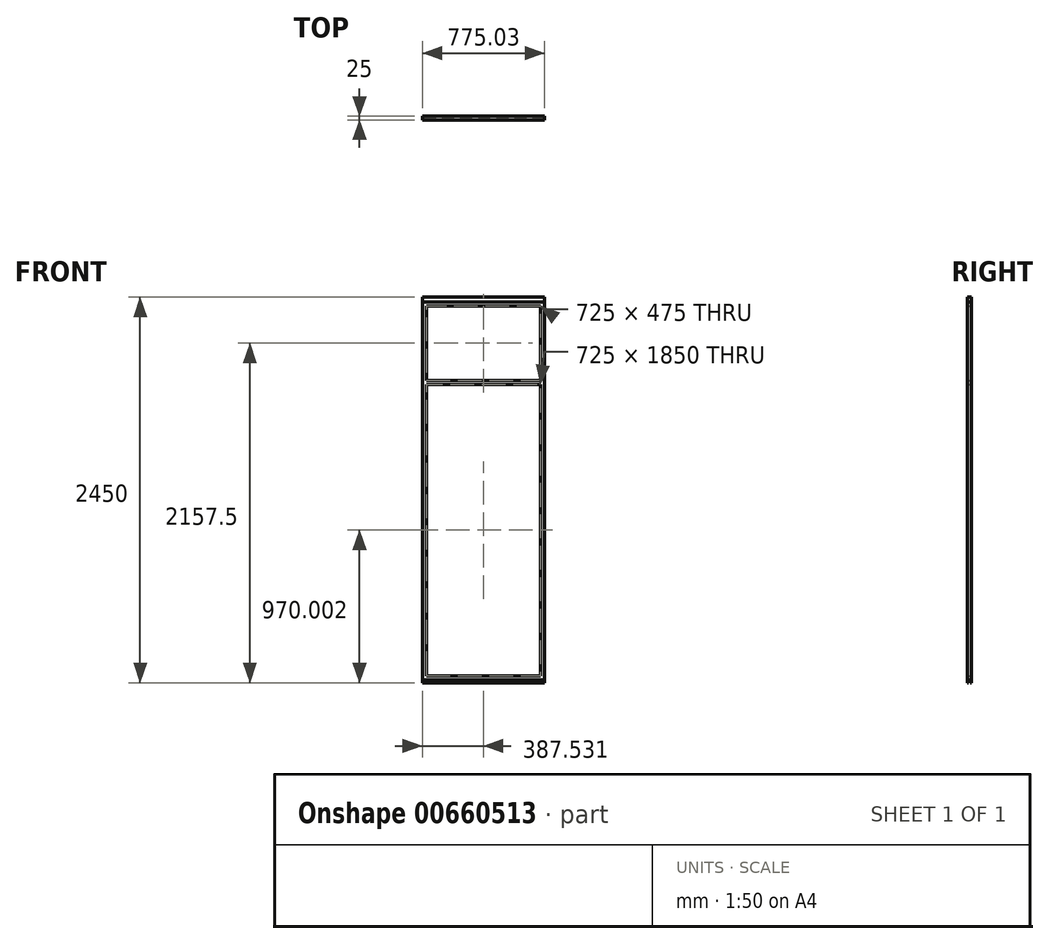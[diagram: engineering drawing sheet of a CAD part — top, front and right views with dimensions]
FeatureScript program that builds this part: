
annotation { "Feature Type Name" : "Feature", "Feature Type Description" : "" }
export const myFeature = defineFeature(function(context is Context, id is Id, definition is map)
    precondition{}
    {
        {
            var Q0;
            Q0=qCreatedBy(makeId("Front.planeOp"),FACE);
            var sketch = newSketch(context, id + "F0", { "sketchPlane" : qUnion([Q0])});
            skLineSegment(sketch, "E0", {"start": v(-1447.05, 238.44) * mm, "end": v(-722.05, 238.44) * mm});
            skLineSegment(sketch, "E1", {"start": v(-1472.05, 738.44) * mm, "end": v(-1472.05, 238.44) * mm});
            skLineSegment(sketch, "E2", {"start": v(-1472.05, 238.44) * mm, "end": v(-1472.05, -1661.56) * mm});
            skPoint(sketch, "E3", {"position": v(-697.05, 738.44) * mm});
            skLineSegment(sketch, "E4", {"start": v(-1472.05, 738.44) * mm, "end": v(-697.05, 738.44) * mm});
            skLineSegment(sketch, "E5", {"start": v(-697.05, 713.44) * mm, "end": v(-697.05, 238.44) * mm});
            skLineSegment(sketch, "E6.0", {"start": v(-1447.05, 713.44) * mm, "end": v(-1447.05, 238.44) * mm});
            skLineSegment(sketch, "E6.1", {"start": v(-1447.05, 213.44) * mm, "end": v(-1447.05, -1636.56) * mm});
            skLineSegment(sketch, "E6.5", {"start": v(-1447.05, 713.44) * mm, "end": v(-722.05, 713.44) * mm});
            skLineSegment(sketch, "E6.6", {"start": v(-1447.05, -1636.56) * mm, "end": v(-722.05, -1636.56) * mm});
            skLineSegment(sketch, "E7.0", {"start": v(-722.05, 713.44) * mm, "end": v(-722.05, 238.44) * mm});
            skLineSegment(sketch, "E8.0", {"start": v(-1447.05, 213.44) * mm, "end": v(-722.05, 213.44) * mm});
            skLineSegment(sketch, "E9.trimOffspring", {"start": v(-697.05, 213.44) * mm, "end": v(-697.05, -1636.56) * mm});
            skLineSegment(sketch, "E10.trimOffspring", {"start": v(-722.05, 213.44) * mm, "end": v(-722.05, -1636.56) * mm});
            skLineSegment(sketch, "E11", {"start": v(-1472.05, -1661.56) * mm, "end": v(-697.05, -1661.56) * mm});
            skLineSegment(sketch, "E12", {"start": v(-697.05, -1636.56) * mm, "end": v(-697.05, -1661.56) * mm});
            skLineSegment(sketch, "E13", {"start": v(-697.05, 738.44) * mm, "end": v(-697.05, 713.44) * mm});
            skLineSegment(sketch, "E14", {"start": v(-697.05, 238.44) * mm, "end": v(-697.05, 213.44) * mm});
            skSolve(sketch);
        }
        {
            var Q0;
            Q0=makeQuery(id+"F0.imprint","IMPRINT",FACE,{"disambiguationData":[TD([[makeQuery(id+"F0.imprint","IMPRINT",EDGE,{"derivedFrom":sQuery(id+"F0.wireOp",EDGE,"E0")}),-1.0]])]});
            extrude(context, id + "F1", {"entities" : qUnion([Q0]), "depth" : 25 * mm, "offsetDistance" : 25 * mm});
        }
        {
            var Q0;
            Q0=makeQuery(id+"F1.opExtrude","CAP_FACE",FACE,{"disambiguationData":[OSD([sQuery(id+"F0.wireOp",EDGE,"E0"),sQuery(id+"F0.wireOp",EDGE,"E1"),sQuery(id+"F0.wireOp",EDGE,"E2"),sQuery(id+"F0.wireOp",EDGE,"E4"),sQuery(id+"F0.wireOp",EDGE,"E5"),sQuery(id+"F0.wireOp",EDGE,"E6.0"),sQuery(id+"F0.wireOp",EDGE,"E6.1"),sQuery(id+"F0.wireOp",EDGE,"E6.5"),sQuery(id+"F0.wireOp",EDGE,"E6.6"),sQuery(id+"F0.wireOp",EDGE,"E7.0"),sQuery(id+"F0.wireOp",EDGE,"E8.0"),sQuery(id+"F0.wireOp",EDGE,"E9.trimOffspring"),sQuery(id+"F0.wireOp",EDGE,"E10.trimOffspring"),sQuery(id+"F0.wireOp",EDGE,"E11"),sQuery(id+"F0.wireOp",EDGE,"E12"),sQuery(id+"F0.wireOp",EDGE,"E13"),sQuery(id+"F0.wireOp",EDGE,"E14")])],"isStart":true});
            var sketch = newSketch(context, id + "F2", { "sketchPlane" : qUnion([Q0])});
            skLineSegment(sketch, "E15.bottom", {"start": v(697.05, -1661.56) * mm, "end": v(1472.08, -1661.56) * mm});
            skLineSegment(sketch, "E15.top", {"start": v(697.05, -1681.56) * mm, "end": v(1472.08, -1681.56) * mm});
            skLineSegment(sketch, "E15.left", {"start": v(697.05, -1661.56) * mm, "end": v(697.05, -1681.56) * mm});
            skLineSegment(sketch, "E15.right", {"start": v(1472.08, -1661.56) * mm, "end": v(1472.08, -1681.56) * mm});
            skSolve(sketch);
        }
        {
            var Q0;
            Q0 = qSketchRegion(id + "F2", true);
            extrude(context, id + "F3", {"entities" : qUnion([Q0]), "oppositeDirection" : true, "depth" : 25 * mm, "offsetDistance" : 25 * mm});
        }
        {
            var Q0;
            Q0=makeQuery(id+"F3.opExtrude","SWEPT_FACE",FACE,{"disambiguationData":[OSD([sQuery(id+"F2.wireOp",EDGE,"E15.right")])]});
            var sketch = newSketch(context, id + "F4", { "sketchPlane" : qUnion([Q0])});
            skLineSegment(sketch, "E16", {"start": v(12.5, -1681.56) * mm, "end": v(12.5, -1666.56) * mm, "construction": true});
            skLineSegment(sketch, "E17.bottom", {"start": v(6.5, -1666.56) * mm, "end": v(18.5, -1666.56) * mm});
            skLineSegment(sketch, "E17.top", {"start": v(6.5, -1681.56) * mm, "end": v(18.5, -1681.56) * mm});
            skLineSegment(sketch, "E17.left", {"start": v(6.5, -1666.56) * mm, "end": v(6.5, -1681.56) * mm});
            skLineSegment(sketch, "E17.right", {"start": v(18.5, -1666.56) * mm, "end": v(18.5, -1681.56) * mm});
            skPoint(sketch, "E18", {"position": v(12.5, -1681.56) * mm});
            skSolve(sketch);
        }
        {
            var Q0;
            Q0 = qSketchRegion(id + "F4", true);
            extrude(context, id + "F5", {"entities" : qUnion([Q0]), "operationType" : NewBodyOperationType.REMOVE, "endBound" : BoundingType.THROUGH_ALL, "oppositeDirection" : true, "depth" : 25 * mm, "offsetDistance" : 25 * mm});
        }
        {
            var Q0;
            Q0=makeQuery(id+"F1.opExtrude","CAP_FACE",FACE,{"disambiguationData":[OSD([sQuery(id+"F0.wireOp",EDGE,"E0"),sQuery(id+"F0.wireOp",EDGE,"E1"),sQuery(id+"F0.wireOp",EDGE,"E2"),sQuery(id+"F0.wireOp",EDGE,"E4"),sQuery(id+"F0.wireOp",EDGE,"E5"),sQuery(id+"F0.wireOp",EDGE,"E6.0"),sQuery(id+"F0.wireOp",EDGE,"E6.1"),sQuery(id+"F0.wireOp",EDGE,"E6.5"),sQuery(id+"F0.wireOp",EDGE,"E6.6"),sQuery(id+"F0.wireOp",EDGE,"E7.0"),sQuery(id+"F0.wireOp",EDGE,"E8.0"),sQuery(id+"F0.wireOp",EDGE,"E9.trimOffspring"),sQuery(id+"F0.wireOp",EDGE,"E10.trimOffspring"),sQuery(id+"F0.wireOp",EDGE,"E11"),sQuery(id+"F0.wireOp",EDGE,"E12"),sQuery(id+"F0.wireOp",EDGE,"E13"),sQuery(id+"F0.wireOp",EDGE,"E14")])],"isStart":false});
            var sketch = newSketch(context, id + "F6", { "sketchPlane" : qUnion([Q0])});
            skLineSegment(sketch, "E19.bottom", {"start": v(-1472.05, 738.44) * mm, "end": v(-697.05, 738.44) * mm});
            skLineSegment(sketch, "E19.top", {"start": v(-1472.05, 738.44) * mm, "end": v(-697.05, 738.44) * mm});
            skLineSegment(sketch, "E19.left", {"start": v(-1472.05, 738.44) * mm, "end": v(-1472.05, 738.44) * mm});
            skLineSegment(sketch, "E19.right", {"start": v(-697.05, 738.44) * mm, "end": v(-697.05, 738.44) * mm});
            skLineSegment(sketch, "E20.bottom", {"start": v(-697.05, 768.44) * mm, "end": v(-1472.05, 768.44) * mm});
            skLineSegment(sketch, "E20.top", {"start": v(-697.05, 738.44) * mm, "end": v(-1472.05, 738.44) * mm});
            skLineSegment(sketch, "E20.left", {"start": v(-697.05, 768.44) * mm, "end": v(-697.05, 738.44) * mm});
            skLineSegment(sketch, "E20.right", {"start": v(-1472.05, 768.44) * mm, "end": v(-1472.05, 738.44) * mm});
            skSolve(sketch);
        }
        {
            var Q0;
            Q0=makeQuery(id+"F6.imprint","IMPRINT",FACE,{"disambiguationData":[TD([[makeQuery(id+"F6.imprint","IMPRINT",EDGE,{"derivedFrom":sQuery(id+"F6.wireOp",EDGE,"E20.bottom")}),1.0]])]});
            extrude(context, id + "F7", {"entities" : qUnion([Q0]), "oppositeDirection" : true, "depth" : 25 * mm, "offsetDistance" : 25 * mm});
        }
    });
